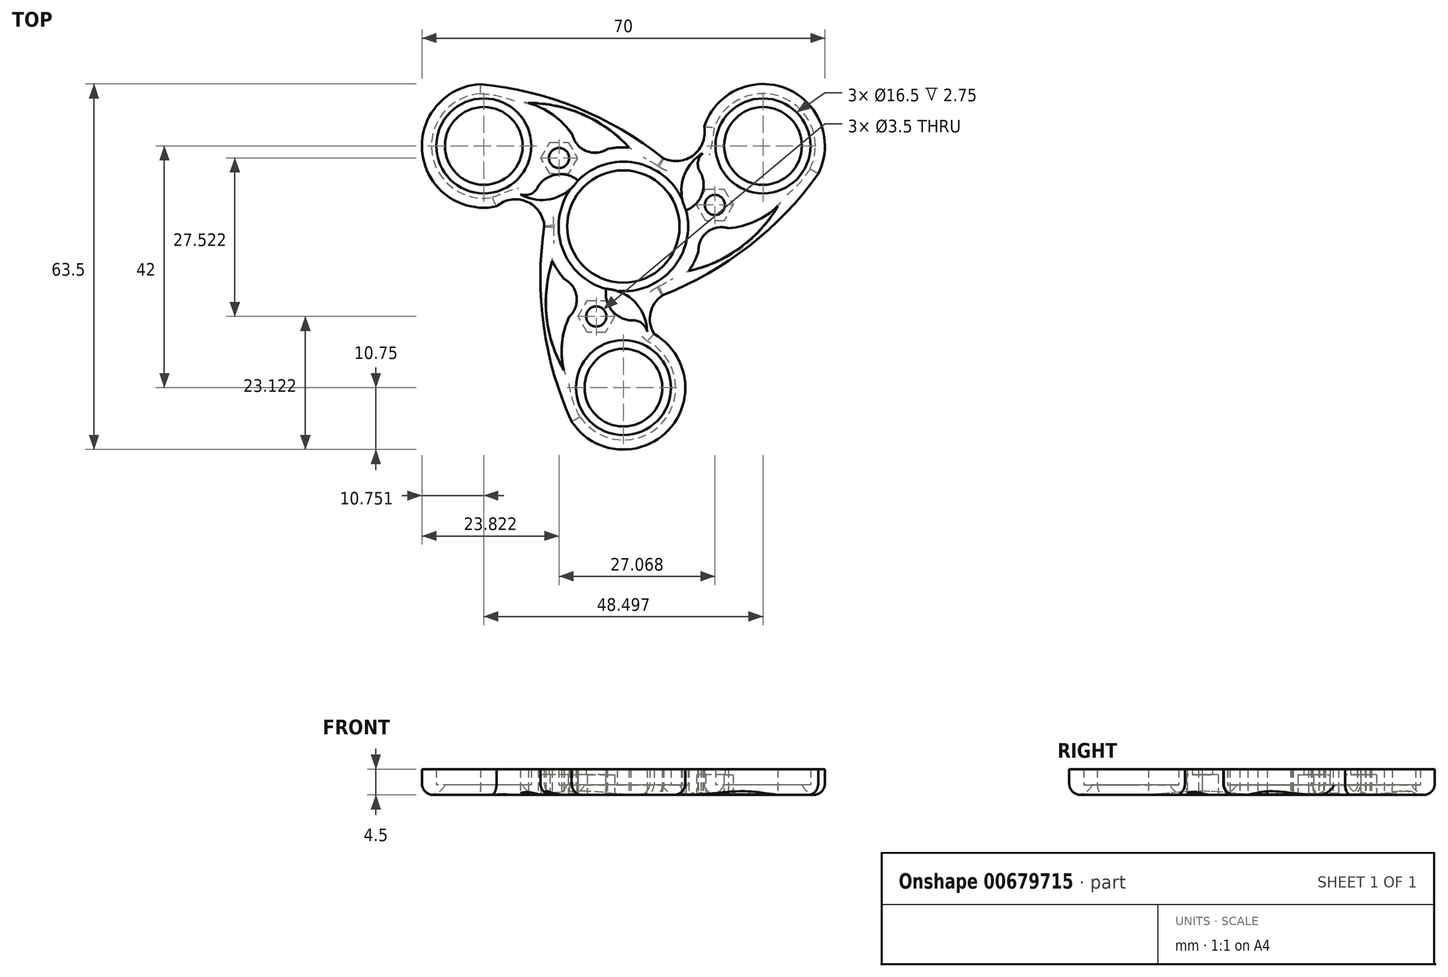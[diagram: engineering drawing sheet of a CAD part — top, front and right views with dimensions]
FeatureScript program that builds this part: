
annotation { "Feature Type Name" : "Feature", "Feature Type Description" : "" }
export const myFeature = defineFeature(function(context is Context, id is Id, definition is map)
    precondition{}
    {
        {
            assignVariable(context, id + "F0", {"name" : "OuterBearingHeight", "anyValue" : 5});
        }
        {
            assignVariable(context, id + "F1", {"name" : "CenterBearingHeight", "anyValue" : 7});
        }
        {
            var Q0;
            Q0=qCreatedBy(makeId("Top.planeOp"),FACE);
            var sketch = newSketch(context, id + "F2", { "sketchPlane" : qUnion([Q0])});
            skCircle(sketch, "E0", {"center": v(0, 0) * mm, "radius": 11.25 * mm});
            skCircle(sketch, "E1", {"center": v(0, 0) * mm, "radius": 9.75 * mm});
            skCircle(sketch, "E2", {"center": v(0, 0) * mm, "radius": 13.75 * mm});
            skCircle(sketch, "E3", {"center": v(0, -28) * mm, "radius": 10.75 * mm});
            skArc(sketch, "E4", {"start": v(-13.75, 0) * mm, "mid": v(-13.84, -17.29) * mm, "end": v(-9, -33.88) * mm});
            skArc(sketch, "E5", {"start": v(6.75, -11.98) * mm, "mid": v(4.65, -16.78) * mm, "end": v(8, -20.82) * mm});
            skPoint(sketch, "E6.center", {"position": v(0.04, 0.07) * mm});
            skCircle(sketch, "E7.cCircle", {"center": v(-4.71, -15.63) * mm, "radius": 2.75 * mm, "construction": true});
            skLineSegment(sketch, "E7.0", {"start": v(-3.12, -18.38) * mm, "end": v(-6.3, -18.38) * mm});
            skLineSegment(sketch, "E7.1", {"start": v(-6.3, -18.38) * mm, "end": v(-7.89, -15.63) * mm});
            skLineSegment(sketch, "E7.2", {"start": v(-7.89, -15.63) * mm, "end": v(-6.3, -12.88) * mm});
            skLineSegment(sketch, "E7.3", {"start": v(-6.3, -12.88) * mm, "end": v(-3.12, -12.88) * mm});
            skLineSegment(sketch, "E7.4", {"start": v(-3.12, -12.88) * mm, "end": v(-1.54, -15.63) * mm});
            skLineSegment(sketch, "E7.5", {"start": v(-1.54, -15.63) * mm, "end": v(-3.12, -18.38) * mm});
            skPoint(sketch, "E7.0.midPoint", {"position": v(-4.71, -18.38) * mm});
            skLineSegment(sketch, "E8", {"start": v(-4.71, -15.63) * mm, "end": v(-4.71, -12.92) * mm, "construction": true});
            skLineSegment(sketch, "E9", {"start": v(-4.71, -15.63) * mm, "end": v(-4.71, -18.34) * mm, "construction": true});
            skLineSegment(sketch, "E10", {"start": v(-4.71, -15.63) * mm, "end": v(-14.05, -15.63) * mm, "construction": true});
            skLineSegment(sketch, "E11", {"start": v(-4.71, -15.63) * mm, "end": v(4.63, -15.63) * mm, "construction": true});
            skCircle(sketch, "E12", {"center": v(-4.71, -15.63) * mm, "radius": 1.75 * mm});
            skArc(sketch, "E13", {"start": v(-12.37, -6) * mm, "mid": v(-13.33, -15.72) * mm, "end": v(-10.33, -25.02) * mm});
            skArc(sketch, "E14", {"start": v(-9.38, -15.63) * mm, "mid": v(-10.67, -20.24) * mm, "end": v(-10.33, -25.02) * mm});
            skArc(sketch, "E15", {"start": v(-9.38, -15.63) * mm, "mid": v(-8.13, -12.14) * mm, "end": v(-10.29, -9.12) * mm});
            skArc(sketch, "E16", {"start": v(4.11, -18.27) * mm, "mid": v(2.02, -13.15) * mm, "end": v(-3, -10.84) * mm});
            skArc(sketch, "E17", {"start": v(4.11, -18.27) * mm, "mid": v(3.08, -16.71) * mm, "end": v(1.26, -16.32) * mm});
            skArc(sketch, "E18", {"start": v(-3, -10.84) * mm, "mid": v(-2.06, -14.5) * mm, "end": v(1.26, -16.32) * mm});
            skCircle(sketch, "E19", {"center": v(0, -28) * mm, "radius": 8.25 * mm});
            skCircle(sketch, "E20", {"center": v(0, -28) * mm, "radius": 6.75 * mm});
            skArc(sketch, "E21.1.0", {"start": v(11.38, -7.71) * mm, "mid": v(20.28, -3.68) * mm, "end": v(26.83, 3.56) * mm});
            skLineSegment(sketch, "E21.1.1", {"start": v(17.48, 0.98) * mm, "end": v(14.3, 0.98) * mm});
            skLineSegment(sketch, "E21.1.2", {"start": v(14.3, 0.98) * mm, "end": v(12.71, 3.73) * mm});
            skCircle(sketch, "E21.1.3", {"center": v(15.89, 3.73) * mm, "radius": 2.75 * mm, "construction": true});
            skCircle(sketch, "E21.1.4", {"center": v(15.89, 3.73) * mm, "radius": 1.75 * mm});
            skLineSegment(sketch, "E21.1.5", {"start": v(19.07, 3.73) * mm, "end": v(17.48, 0.98) * mm});
            skLineSegment(sketch, "E21.1.6", {"start": v(17.48, 6.48) * mm, "end": v(19.07, 3.73) * mm});
            skLineSegment(sketch, "E21.1.7", {"start": v(14.3, 6.48) * mm, "end": v(17.48, 6.48) * mm});
            skLineSegment(sketch, "E21.1.8", {"start": v(12.71, 3.73) * mm, "end": v(14.3, 6.48) * mm});
            skArc(sketch, "E21.1.9", {"start": v(10.89, 2.82) * mm, "mid": v(13.6, 5.47) * mm, "end": v(13.5, 9.25) * mm});
            skArc(sketch, "E21.1.10", {"start": v(13.76, 12.7) * mm, "mid": v(10.38, 8.33) * mm, "end": v(10.89, 2.82) * mm});
            skArc(sketch, "E21.1.11", {"start": v(7, 11.84) * mm, "mid": v(12.2, 12.42) * mm, "end": v(14.03, 17.34) * mm});
            skCircle(sketch, "E21.1.12", {"center": v(24.25, 14) * mm, "radius": 10.75 * mm});
            skCircle(sketch, "E21.1.13", {"center": v(24.25, 14) * mm, "radius": 8.25 * mm});
            skCircle(sketch, "E21.1.14", {"center": v(24.25, 14) * mm, "radius": 6.75 * mm});
            skArc(sketch, "E21.1.15", {"start": v(13.76, 12.7) * mm, "mid": v(12.93, 11.02) * mm, "end": v(13.5, 9.25) * mm});
            skArc(sketch, "E21.1.16", {"start": v(6.87, -11.9) * mm, "mid": v(21.89, -3.34) * mm, "end": v(33.84, 9.15) * mm});
            skArc(sketch, "E21.1.17", {"start": v(18.22, -0.31) * mm, "mid": v(14.58, -0.98) * mm, "end": v(13.04, -4.35) * mm});
            skArc(sketch, "E21.1.18", {"start": v(18.22, -0.31) * mm, "mid": v(22.86, 0.88) * mm, "end": v(26.83, 3.56) * mm});
            skArc(sketch, "E21.2.0", {"start": v(1, 13.71) * mm, "mid": v(-6.95, 19.4) * mm, "end": v(-16.5, 21.45) * mm});
            skLineSegment(sketch, "E21.2.1", {"start": v(-9.6, 14.64) * mm, "end": v(-8, 11.9) * mm});
            skLineSegment(sketch, "E21.2.2", {"start": v(-8, 11.9) * mm, "end": v(-9.6, 9.14) * mm});
            skCircle(sketch, "E21.2.3", {"center": v(-11.18, 11.9) * mm, "radius": 2.75 * mm, "construction": true});
            skCircle(sketch, "E21.2.4", {"center": v(-11.18, 11.9) * mm, "radius": 1.75 * mm});
            skLineSegment(sketch, "E21.2.5", {"start": v(-12.77, 14.64) * mm, "end": v(-9.6, 14.64) * mm});
            skLineSegment(sketch, "E21.2.6", {"start": v(-14.35, 11.9) * mm, "end": v(-12.77, 14.64) * mm});
            skLineSegment(sketch, "E21.2.7", {"start": v(-12.77, 9.14) * mm, "end": v(-14.35, 11.9) * mm});
            skLineSegment(sketch, "E21.2.8", {"start": v(-9.6, 9.14) * mm, "end": v(-12.77, 9.14) * mm});
            skArc(sketch, "E21.2.9", {"start": v(-7.89, 8.02) * mm, "mid": v(-11.53, 9.04) * mm, "end": v(-14.76, 7.07) * mm});
            skArc(sketch, "E21.2.10", {"start": v(-17.87, 5.57) * mm, "mid": v(-12.4, 4.82) * mm, "end": v(-7.89, 8.02) * mm});
            skArc(sketch, "E21.2.11", {"start": v(-13.75, 0.14) * mm, "mid": v(-16.86, 4.36) * mm, "end": v(-22.03, 3.48) * mm});
            skCircle(sketch, "E21.2.12", {"center": v(-24.25, 14) * mm, "radius": 10.75 * mm});
            skCircle(sketch, "E21.2.13", {"center": v(-24.25, 14) * mm, "radius": 8.25 * mm});
            skCircle(sketch, "E21.2.14", {"center": v(-24.25, 14) * mm, "radius": 6.75 * mm});
            skArc(sketch, "E21.2.15", {"start": v(-17.87, 5.57) * mm, "mid": v(-16.01, 5.7) * mm, "end": v(-14.76, 7.07) * mm});
            skArc(sketch, "E21.2.16", {"start": v(6.87, 11.9) * mm, "mid": v(-8.05, 20.63) * mm, "end": v(-24.84, 24.73) * mm});
            skArc(sketch, "E21.2.17", {"start": v(-8.84, 15.94) * mm, "mid": v(-6.44, 13.11) * mm, "end": v(-2.75, 13.47) * mm});
            skArc(sketch, "E21.2.18", {"start": v(-8.84, 15.94) * mm, "mid": v(-12.2, 19.36) * mm, "end": v(-16.5, 21.45) * mm});
            skSolve(sketch);
        }
        {
            var Q0;
            {var subQ0=sQuery(id+"F2.wireOp",EDGE,"E7.1");Q0=makeQuery(id+"F2.imprint","IMPRINT",FACE,{"disambiguationData":[TD([[makeQuery(id+"F2.imprint","IMPRINT",EDGE,{"derivedFrom":subQ0}),1.0]])]});}
            var Q1;
            {var subQ5=sQuery(id+"F2.wireOp",EDGE,"E5");Q1=makeQuery(id+"F2.imprint","IMPRINT",FACE,{"disambiguationData":[TD([[makeQuery(id+"F2.imprint","IMPRINT",EDGE,{"derivedFrom":subQ5}),-1.0]])]});}
            var Q2;
            {var subQ0=sQuery(id+"F2.wireOp",EDGE,"f691ac80-1c01-42f0-a88e-231e112aa074.1.8");Q2=makeQuery(id+"F2.imprint","IMPRINT",FACE,{"disambiguationData":[TD([[makeQuery(id+"F2.imprint","IMPRINT",EDGE,{"derivedFrom":subQ0}),1.0]])]});}
            var Q3;
            {var subQ1=sQuery(id+"F2.wireOp",EDGE,"f691ac80-1c01-42f0-a88e-231e112aa074.1.0");Q3=makeQuery(id+"F2.imprint","IMPRINT",FACE,{"disambiguationData":[TD([[makeQuery(id+"F2.imprint","IMPRINT",EDGE,{"derivedFrom":subQ1}),-1.0]])]});}
            var Q4;
            {var subQ0=sQuery(id+"F2.wireOp",EDGE,"f691ac80-1c01-42f0-a88e-231e112aa074.2.8");Q4=makeQuery(id+"F2.imprint","IMPRINT",FACE,{"disambiguationData":[TD([[makeQuery(id+"F2.imprint","IMPRINT",EDGE,{"derivedFrom":subQ0}),1.0]])]});}
            var Q5;
            Q5=makeQuery(id+"F2.imprint","IMPRINT",FACE,{"disambiguationData":[TD([[makeQuery(id+"F2.imprint","IMPRINT",EDGE,{"derivedFrom":sQuery(id+"F2.wireOp",EDGE,"f691ac80-1c01-42f0-a88e-231e112aa074.2.2")}),-1.0]])]});
            var Q6;
            Q6=makeQuery(id+"F2.imprint","IMPRINT",FACE,{"disambiguationData":[TD([[makeQuery(id+"F2.imprint","IMPRINT",EDGE,{"derivedFrom":sQuery(id+"F2.wireOp",EDGE,"f691ac80-1c01-42f0-a88e-231e112aa074.1.2")}),-1.0]])]});
            var Q7;
            {var subQ1=sQuery(id+"F2.wireOp",EDGE,"f691ac80-1c01-42f0-a88e-231e112aa074.2.0");Q7=makeQuery(id+"F2.imprint","IMPRINT",FACE,{"disambiguationData":[TD([[makeQuery(id+"F2.imprint","IMPRINT",EDGE,{"derivedFrom":subQ1}),-1.0]])]});}
            var Q8;
            Q8=makeQuery(id+"F2.imprint","IMPRINT",FACE,{"disambiguationData":[TD([[makeQuery(id+"F2.imprint","IMPRINT",EDGE,{"derivedFrom":sQuery(id+"F2.wireOp",EDGE,"aKZDALUb-4dyq-ynNd-1TMt-uQF9IDW9dU3x")}),-1.0]])]});
            var Q9;
            {var subQ0=sQuery(id+"F2.wireOp",EDGE,"BNeyDjp7-idxR-Yro0-WZsy-1JtXtv3nSXo7");Q9=makeQuery(id+"F2.imprint","IMPRINT",FACE,{"disambiguationData":[TD([[makeQuery(id+"F2.imprint","IMPRINT",EDGE,{"derivedFrom":subQ0}),1.0]])]});}
            var Q10;
            {var subQ0=sQuery(id+"F2.wireOp",EDGE,"8gaKkmaj-PT3W-1uV4-PrTw-aFj1ESdI5pcj");var subQ1=sQuery(id+"F2.wireOp",EDGE,"E4");var subQ2=makeQuery(id+"F2.imprint","INTERSECT",VERTEX,{"disambiguationData":[OD(0.0)],"derivedFrom":[subQ1,subQ0]});Q10=makeQuery(id+"F2.imprint","IMPRINT",FACE,{"disambiguationData":[TD([[makeQuery(id+"F2.imprint","IMPRINT",EDGE,{"disambiguationData":[TD([[subQ2,-1.0]])],"derivedFrom":subQ1}),-1.0]])]});}
            var Q11;
            {var subQ3=sQuery(id+"F2.wireOp",EDGE,"E13");Q11=makeQuery(id+"F2.imprint","IMPRINT",FACE,{"disambiguationData":[TD([[makeQuery(id+"F2.imprint","IMPRINT",EDGE,{"derivedFrom":subQ3}),-1.0]])]});}
            var Q12;
            {var subQ5=sQuery(id+"F2.wireOp",EDGE,"yW5sj1OK-dV5J-gnst-7nq6-E0PAgaZ6P3tT");Q12=makeQuery(id+"F2.imprint","IMPRINT",FACE,{"disambiguationData":[TD([[makeQuery(id+"F2.imprint","IMPRINT",EDGE,{"derivedFrom":subQ5}),1.0]])]});}
            var Q13;
            {var subQ0=sQuery(id+"F2.wireOp",EDGE,"E5");var subQ1=sQuery(id+"F2.wireOp",EDGE,"E3");var subQ2=makeQuery(id+"F2.imprint","INTERSECT",VERTEX,{"disambiguationData":[OD(0.0)],"derivedFrom":[subQ1,subQ0]});Q13=makeQuery(id+"F2.imprint","IMPRINT",FACE,{"disambiguationData":[TD([[makeQuery(id+"F2.imprint","IMPRINT",EDGE,{"disambiguationData":[TD([[subQ2,-1.0]])],"derivedFrom":subQ1}),1.0]])]});}
            var Q14;
            {var subQ1=sQuery(id+"F2.wireOp",EDGE,"E7.4");var subQ3=sQuery(id+"F2.wireOp",EDGE,"E2");var subQ4=makeQuery(id+"F2.imprint","INTERSECT",VERTEX,{"derivedFrom":[subQ3,subQ1]});Q14=makeQuery(id+"F2.imprint","IMPRINT",FACE,{"disambiguationData":[TD([[makeQuery(id+"F2.imprint","IMPRINT",EDGE,{"disambiguationData":[TD([[subQ4,-1.0]])],"derivedFrom":subQ3}),-1.0]])]});}
            var Q15;
            {var subQ0=sQuery(id+"F2.wireOp",EDGE,"E16");var subQ1=sQuery(id+"F2.wireOp",EDGE,"E5");var subQ2=makeQuery(id+"F2.imprint","INTERSECT",VERTEX,{"disambiguationData":[OD(0.0)],"derivedFrom":[subQ1,subQ0]});Q15=makeQuery(id+"F2.imprint","IMPRINT",FACE,{"disambiguationData":[TD([[makeQuery(id+"F2.imprint","IMPRINT",EDGE,{"disambiguationData":[TD([[subQ2,-1.0]])],"derivedFrom":subQ1}),1.0]])]});}
            var Q16;
            Q16=makeQuery(id+"F2.imprint","IMPRINT",FACE,{"disambiguationData":[TD([[makeQuery(id+"F2.imprint","IMPRINT",EDGE,{"derivedFrom":sQuery(id+"F2.wireOp",EDGE,"E19")}),-1.0]])]});
            var Q17;
            {var subQ3=sQuery(id+"F2.wireOp",EDGE,"E2");var subQ7=makeQuery(id+"F2.imprint","INTERSECT",VERTEX,{"derivedFrom":[subQ3,sQuery(id+"F2.wireOp",EDGE,"E4")]});Q17=makeQuery(id+"F2.imprint","IMPRINT",FACE,{"disambiguationData":[TD([[makeQuery(id+"F2.imprint","IMPRINT",EDGE,{"disambiguationData":[TD([[subQ7,-1.0]])],"derivedFrom":subQ3}),1.0]])]});}
            var Q18;
            {var subQ1=sQuery(id+"F2.wireOp",EDGE,"E2");var subQ5=sQuery(id+"F2.wireOp",EDGE,"E21.1.8");var subQ15=makeQuery(id+"F2.imprint","INTERSECT",VERTEX,{"derivedFrom":[subQ1,subQ5]});Q18=makeQuery(id+"F2.imprint","IMPRINT",FACE,{"disambiguationData":[TD([[makeQuery(id+"F2.imprint","IMPRINT",EDGE,{"disambiguationData":[TD([[subQ15,-1.0]])],"derivedFrom":subQ1}),1.0]])]});}
            var Q19;
            {var subQ0=sQuery(id+"F2.wireOp",EDGE,"E21.1.0");Q19=makeQuery(id+"F2.imprint","IMPRINT",FACE,{"disambiguationData":[TD([[makeQuery(id+"F2.imprint","IMPRINT",EDGE,{"derivedFrom":subQ0}),-1.0]])]});}
            var Q20;
            {var subQ6=sQuery(id+"F2.wireOp",EDGE,"E21.1.1");Q20=makeQuery(id+"F2.imprint","IMPRINT",FACE,{"disambiguationData":[TD([[makeQuery(id+"F2.imprint","IMPRINT",EDGE,{"derivedFrom":subQ6}),1.0]])]});}
            var Q21;
            {var subQ3=sQuery(id+"F2.wireOp",EDGE,"E2");var subQ5=sQuery(id+"F2.wireOp",EDGE,"E21.1.8");var subQ6=makeQuery(id+"F2.imprint","INTERSECT",VERTEX,{"derivedFrom":[subQ3,subQ5]});Q21=makeQuery(id+"F2.imprint","IMPRINT",FACE,{"disambiguationData":[TD([[makeQuery(id+"F2.imprint","IMPRINT",EDGE,{"disambiguationData":[TD([[subQ6,-1.0]])],"derivedFrom":subQ3}),-1.0]])]});}
            var Q22;
            {var subQ0=sQuery(id+"F2.wireOp",EDGE,"E21.1.11");var subQ1=sQuery(id+"F2.wireOp",EDGE,"E2");var subQ2=makeQuery(id+"F2.imprint","INTERSECT",VERTEX,{"derivedFrom":[subQ1,subQ0]});Q22=makeQuery(id+"F2.imprint","IMPRINT",FACE,{"disambiguationData":[TD([[makeQuery(id+"F2.imprint","IMPRINT",EDGE,{"disambiguationData":[TD([[subQ2,1.0]])],"derivedFrom":subQ1}),-1.0]])]});}
            var Q23;
            {var subQ3=sQuery(id+"F2.wireOp",EDGE,"E2");var subQ16=makeQuery(id+"F2.imprint","INTERSECT",VERTEX,{"derivedFrom":[subQ3,sQuery(id+"F2.wireOp",EDGE,"E21.1.11")]});Q23=makeQuery(id+"F2.imprint","IMPRINT",FACE,{"disambiguationData":[TD([[makeQuery(id+"F2.imprint","IMPRINT",EDGE,{"disambiguationData":[TD([[subQ16,1.0]])],"derivedFrom":subQ3}),1.0]])]});}
            var Q24;
            Q24=makeQuery(id+"F2.imprint","IMPRINT",FACE,{"disambiguationData":[TD([[makeQuery(id+"F2.imprint","IMPRINT",EDGE,{"derivedFrom":sQuery(id+"F2.wireOp",EDGE,"E21.1.13")}),-1.0]])]});
            var Q25;
            Q25=makeQuery(id+"F2.imprint","IMPRINT",FACE,{"disambiguationData":[TD([[makeQuery(id+"F2.imprint","IMPRINT",EDGE,{"derivedFrom":sQuery(id+"F2.wireOp",EDGE,"E21.2.13")}),-1.0]])]});
            var Q26;
            {var subQ1=sQuery(id+"F2.wireOp",EDGE,"E21.2.1");Q26=makeQuery(id+"F2.imprint","IMPRINT",FACE,{"disambiguationData":[TD([[makeQuery(id+"F2.imprint","IMPRINT",EDGE,{"derivedFrom":subQ1}),1.0]])]});}
            var Q27;
            {var subQ0=sQuery(id+"F2.wireOp",EDGE,"E21.2.0");Q27=makeQuery(id+"F2.imprint","IMPRINT",FACE,{"disambiguationData":[TD([[makeQuery(id+"F2.imprint","IMPRINT",EDGE,{"derivedFrom":subQ0}),-1.0]])]});}
            var Q28;
            {var subQ0=sQuery(id+"F2.wireOp",EDGE,"E21.2.11");var subQ1=sQuery(id+"F2.wireOp",EDGE,"E2");var subQ2=makeQuery(id+"F2.imprint","INTERSECT",VERTEX,{"derivedFrom":[subQ1,subQ0]});Q28=makeQuery(id+"F2.imprint","IMPRINT",FACE,{"disambiguationData":[TD([[makeQuery(id+"F2.imprint","IMPRINT",EDGE,{"disambiguationData":[TD([[subQ2,1.0]])],"derivedFrom":subQ1}),-1.0]])]});}
            var Q29;
            {var subQ0=sQuery(id+"F2.wireOp",EDGE,"E21.2.8");var subQ3=sQuery(id+"F2.wireOp",EDGE,"E2");var subQ4=makeQuery(id+"F2.imprint","INTERSECT",VERTEX,{"derivedFrom":[subQ3,subQ0]});Q29=makeQuery(id+"F2.imprint","IMPRINT",FACE,{"disambiguationData":[TD([[makeQuery(id+"F2.imprint","IMPRINT",EDGE,{"disambiguationData":[TD([[subQ4,-1.0]])],"derivedFrom":subQ3}),-1.0]])]});}
            extrude(context, id + "F3", {"entities" : qUnion([Q0, Q1, Q2, Q3, Q4, Q5, Q6, Q7, Q8, Q9, Q10, Q11, Q12, Q13, Q14, Q15, Q16, Q17, Q18, Q19, Q20, Q21, Q22, Q23, Q24, Q25, Q26, Q27, Q28, Q29]), "depth" : ((getVariable(context, 'CenterBearingHeight') / 2) + 1) * mm, "offsetDistance" : 25 * mm});
        }
        {
            var Q0;
            Q0=makeQuery(id+"F2.imprint","IMPRINT",FACE,{"disambiguationData":[TD([[makeQuery(id+"F2.imprint","IMPRINT",EDGE,{"derivedFrom":sQuery(id+"F2.wireOp",EDGE,"f691ac80-1c01-42f0-a88e-231e112aa074.2.2")}),1.0]])]});
            var Q1;
            Q1=makeQuery(id+"F2.imprint","IMPRINT",FACE,{"disambiguationData":[TD([[makeQuery(id+"F2.imprint","IMPRINT",EDGE,{"derivedFrom":sQuery(id+"F2.wireOp",EDGE,"f691ac80-1c01-42f0-a88e-231e112aa074.1.2")}),1.0]])]});
            var Q2;
            Q2=makeQuery(id+"F2.imprint","IMPRINT",FACE,{"disambiguationData":[TD([[makeQuery(id+"F2.imprint","IMPRINT",EDGE,{"derivedFrom":sQuery(id+"F2.wireOp",EDGE,"aKZDALUb-4dyq-ynNd-1TMt-uQF9IDW9dU3x")}),1.0]])]});
            var Q3;
            Q3=makeQuery(id+"F2.imprint","IMPRINT",FACE,{"disambiguationData":[TD([[makeQuery(id+"F2.imprint","IMPRINT",EDGE,{"derivedFrom":sQuery(id+"F2.wireOp",EDGE,"E19")}),1.0]])]});
            var Q4;
            Q4=makeQuery(id+"F2.imprint","IMPRINT",FACE,{"disambiguationData":[TD([[makeQuery(id+"F2.imprint","IMPRINT",EDGE,{"derivedFrom":sQuery(id+"F2.wireOp",EDGE,"E1")}),-1.0]])]});
            var Q5;
            Q5=makeQuery(id+"F2.imprint","IMPRINT",FACE,{"disambiguationData":[TD([[makeQuery(id+"F2.imprint","IMPRINT",EDGE,{"derivedFrom":sQuery(id+"F2.wireOp",EDGE,"E21.2.13")}),1.0]])]});
            var Q6;
            Q6=makeQuery(id+"F2.imprint","IMPRINT",FACE,{"disambiguationData":[TD([[makeQuery(id+"F2.imprint","IMPRINT",EDGE,{"derivedFrom":sQuery(id+"F2.wireOp",EDGE,"E21.1.13")}),1.0]])]});
            extrude(context, id + "F4", {"entities" : qUnion([Q0, Q1, Q2, Q3, Q4, Q5, Q6]), "operationType" : NewBodyOperationType.ADD, "depth" : (((getVariable(context, 'CenterBearingHeight') / 2) + .75) - getVariable(context, 'OuterBearingHeight') / 2) * mm, "offsetDistance" : 25 * mm});
        }
        {
            var Q0;
            {var subQ3=sQuery(id+"F2.wireOp",EDGE,"E2");var subQ5=sQuery(id+"F2.wireOp",EDGE,"E5");var subQ6=makeQuery(id+"F2.imprint","INTERSECT",VERTEX,{"derivedFrom":[subQ3,subQ5]});Q0=makeQuery(id+"F2.imprint","IMPRINT",FACE,{"disambiguationData":[TD([[makeQuery(id+"F2.imprint","IMPRINT",EDGE,{"disambiguationData":[TD([[subQ6,1.0]])],"derivedFrom":subQ3}),-1.0]])]});}
            var Q1;
            {var subQ0=sQuery(id+"F2.wireOp",EDGE,"E7.1");Q1=makeQuery(id+"F2.imprint","IMPRINT",FACE,{"disambiguationData":[TD([[makeQuery(id+"F2.imprint","IMPRINT",EDGE,{"derivedFrom":subQ0}),-1.0]])]});}
            var Q2;
            {var subQ0=sQuery(id+"F2.wireOp",EDGE,"E7.3");var subQ1=sQuery(id+"F2.wireOp",EDGE,"E2");var subQ2=makeQuery(id+"F2.imprint","INTERSECT",VERTEX,{"derivedFrom":[subQ1,subQ0]});Q2=makeQuery(id+"F2.imprint","IMPRINT",FACE,{"disambiguationData":[TD([[makeQuery(id+"F2.imprint","IMPRINT",EDGE,{"disambiguationData":[TD([[subQ2,-1.0]])],"derivedFrom":subQ1}),1.0]])]});}
            var Q3;
            {var subQ0=sQuery(id+"F2.wireOp",EDGE,"E7.5");var subQ1=sQuery(id+"F2.wireOp",EDGE,"E3");var subQ2=makeQuery(id+"F2.imprint","INTERSECT",VERTEX,{"derivedFrom":[subQ1,subQ0]});Q3=makeQuery(id+"F2.imprint","IMPRINT",FACE,{"disambiguationData":[TD([[makeQuery(id+"F2.imprint","IMPRINT",EDGE,{"disambiguationData":[TD([[subQ2,-1.0]])],"derivedFrom":subQ1}),1.0]])]});}
            var Q4;
            {var subQ1=sQuery(id+"F2.wireOp",EDGE,"E21.2.1");Q4=makeQuery(id+"F2.imprint","IMPRINT",FACE,{"disambiguationData":[TD([[makeQuery(id+"F2.imprint","IMPRINT",EDGE,{"derivedFrom":subQ1}),-1.0]])]});}
            var Q5;
            {var subQ0=sQuery(id+"F2.wireOp",EDGE,"E21.2.2");var subQ1=sQuery(id+"F2.wireOp",EDGE,"E2");var subQ2=makeQuery(id+"F2.imprint","INTERSECT",VERTEX,{"derivedFrom":[subQ1,subQ0]});Q5=makeQuery(id+"F2.imprint","IMPRINT",FACE,{"disambiguationData":[TD([[makeQuery(id+"F2.imprint","IMPRINT",EDGE,{"disambiguationData":[TD([[subQ2,-1.0]])],"derivedFrom":subQ1}),1.0]])]});}
            var Q6;
            {var subQ0=sQuery(id+"F2.wireOp",EDGE,"E21.2.7");var subQ1=sQuery(id+"F2.wireOp",EDGE,"E21.2.6");var subQ2=makeQuery(id+"F2.imprint","INTERSECT",VERTEX,{"derivedFrom":[subQ1,subQ0]});Q6=makeQuery(id+"F2.imprint","IMPRINT",FACE,{"disambiguationData":[TD([[makeQuery(id+"F2.imprint","IMPRINT",EDGE,{"disambiguationData":[TD([[subQ2,-1.0]])],"derivedFrom":subQ1}),-1.0]])]});}
            var Q7;
            {var subQ1=sQuery(id+"F2.wireOp",EDGE,"E21.1.1");Q7=makeQuery(id+"F2.imprint","IMPRINT",FACE,{"disambiguationData":[TD([[makeQuery(id+"F2.imprint","IMPRINT",EDGE,{"derivedFrom":subQ1}),-1.0]])]});}
            var Q8;
            {var subQ0=sQuery(id+"F2.wireOp",EDGE,"E21.1.7");var subQ1=sQuery(id+"F2.wireOp",EDGE,"E21.1.6");var subQ2=makeQuery(id+"F2.imprint","INTERSECT",VERTEX,{"derivedFrom":[subQ1,subQ0]});Q8=makeQuery(id+"F2.imprint","IMPRINT",FACE,{"disambiguationData":[TD([[makeQuery(id+"F2.imprint","IMPRINT",EDGE,{"disambiguationData":[TD([[subQ2,-1.0]])],"derivedFrom":subQ1}),-1.0]])]});}
            var Q9;
            {var subQ0=sQuery(id+"F2.wireOp",EDGE,"E21.1.8");var subQ1=sQuery(id+"F2.wireOp",EDGE,"E2");var subQ2=makeQuery(id+"F2.imprint","INTERSECT",VERTEX,{"derivedFrom":[subQ1,subQ0]});Q9=makeQuery(id+"F2.imprint","IMPRINT",FACE,{"disambiguationData":[TD([[makeQuery(id+"F2.imprint","IMPRINT",EDGE,{"disambiguationData":[TD([[subQ2,1.0]])],"derivedFrom":subQ1}),1.0]])]});}
            extrude(context, id + "F5", {"entities" : qUnion([Q0, Q1, Q2, Q3, Q4, Q5, Q6, Q7, Q8, Q9]), "operationType" : NewBodyOperationType.ADD, "depth" : ((getVariable(context, 'CenterBearingHeight') / 2) + 1) * mm, "offsetDistance" : 25 * mm, "hasSecondDirection" : true, "secondDirectionOppositeDirection" : false, "secondDirectionDepth" : 3.5 * mm});
        }
        {
            var Q0;
            Q0=makeQuery(id+"F2.imprint","IMPRINT",FACE,{"disambiguationData":[TD([[makeQuery(id+"F2.imprint","IMPRINT",EDGE,{"derivedFrom":sQuery(id+"F2.wireOp",EDGE,"E0")}),1.0]])]});
            extrude(context, id + "F6", {"entities" : qUnion([Q0]), "operationType" : NewBodyOperationType.ADD, "depth" : 1 * mm, "offsetDistance" : 25 * mm});
        }
        {
            var Q0;
            Q0=makeQuery(id+"F3.opExtrude","CAP_EDGE",EDGE,{"disambiguationData":[OSD([sQuery(id+"F2.wireOp",EDGE,"E21.2.12")])],"isStart":true});
            var Q1;
            Q1=makeQuery(id+"F3.opExtrude","CAP_EDGE",EDGE,{"disambiguationData":[OSD([sQuery(id+"F2.wireOp",EDGE,"E21.2.11")])],"isStart":true});
            var Q2;
            Q2=makeQuery(id+"F3.opExtrude","CAP_EDGE",EDGE,{"disambiguationData":[OSD([sQuery(id+"F2.wireOp",EDGE,"E21.2.16")])],"isStart":true});
            var Q3;
            Q3=makeQuery(id+"F3.opExtrude","CAP_EDGE",EDGE,{"disambiguationData":[OSD([sQuery(id+"F2.wireOp",EDGE,"E21.1.11")])],"isStart":true});
            var Q4;
            Q4=makeQuery(id+"F3.opExtrude","CAP_EDGE",EDGE,{"disambiguationData":[OSD([sQuery(id+"F2.wireOp",EDGE,"E21.1.12")])],"isStart":true});
            var Q5;
            Q5=makeQuery(id+"F3.opExtrude","CAP_EDGE",EDGE,{"disambiguationData":[OSD([sQuery(id+"F2.wireOp",EDGE,"E21.1.16")])],"isStart":true});
            var Q6;
            Q6=makeQuery(id+"F3.opExtrude","CAP_EDGE",EDGE,{"disambiguationData":[OSD([sQuery(id+"F2.wireOp",EDGE,"E5")])],"isStart":true});
            var Q7;
            Q7=makeQuery(id+"F3.opExtrude","CAP_EDGE",EDGE,{"disambiguationData":[OSD([sQuery(id+"F2.wireOp",EDGE,"E3")])],"isStart":true});
            var Q8;
            Q8=makeQuery(id+"F3.opExtrude","CAP_EDGE",EDGE,{"disambiguationData":[OSD([sQuery(id+"F2.wireOp",EDGE,"E4")])],"isStart":true});
            var Q9;
            {var subQ0=sQuery(id+"F2.wireOp",EDGE,"E2");Q9=makeQuery(id+"F3.opExtrude","CAP_EDGE",EDGE,{"disambiguationData":[OSD([subQ0]),TDD([makeQuery(id+"F2.imprint","IMPRINT",EDGE,{"disambiguationData":[TD([[makeQuery(id+"F2.imprint","INTERSECT",VERTEX,{"derivedFrom":[subQ0,sQuery(id+"F2.wireOp",EDGE,"E21.1.11")]}),-1.0]])],"derivedFrom":subQ0})])],"isStart":true});}
            var Q10;
            {var subQ0=sQuery(id+"F2.wireOp",EDGE,"E2");Q10=makeQuery(id+"F3.opExtrude","CAP_EDGE",EDGE,{"disambiguationData":[OSD([subQ0]),TDD([makeQuery(id+"F2.imprint","IMPRINT",EDGE,{"disambiguationData":[TD([[makeQuery(id+"F2.imprint","INTERSECT",VERTEX,{"derivedFrom":[subQ0,sQuery(id+"F2.wireOp",EDGE,"E5")]}),-1.0]])],"derivedFrom":subQ0})])],"isStart":true});}
            var Q11;
            {var subQ0=sQuery(id+"F2.wireOp",EDGE,"E2");Q11=makeQuery(id+"F3.opExtrude","CAP_EDGE",EDGE,{"disambiguationData":[OSD([subQ0]),TDD([makeQuery(id+"F2.imprint","IMPRINT",EDGE,{"disambiguationData":[TD([[makeQuery(id+"F2.imprint","INTERSECT",VERTEX,{"derivedFrom":[subQ0,sQuery(id+"F2.wireOp",EDGE,"E4")]}),1.0]])],"derivedFrom":subQ0})])],"isStart":true});}
            fillet(context, id + "F7", {"entities" : qUnion([Q0, Q1, Q2, Q3, Q4, Q5, Q6, Q7, Q8, Q9, Q10, Q11]), "radius" : 2 * mm, "tangentPropagation" : true, "allowEdgeOverflow" : false});
        }
        {
            var Q0;
            Q0=makeQuery(id+"F4.opExtrude","CAP_EDGE",EDGE,{"disambiguationData":[OSD([sQuery(id+"F2.wireOp",EDGE,"f691ac80-1c01-42f0-a88e-231e112aa074.2.3")])],"isStart":true});
            var Q1;
            Q1=makeQuery(id+"F6.opExtrude","CAP_EDGE",EDGE,{"disambiguationData":[OSD([sQuery(id+"F2.wireOp",EDGE,"E1")])],"isStart":true});
            var Q2;
            Q2=makeQuery(id+"F4.opExtrude","CAP_EDGE",EDGE,{"disambiguationData":[OSD([sQuery(id+"F2.wireOp",EDGE,"udslHx3o-LPzl-F921-wRQS-P6q11kkCxCmo")])],"isStart":true});
            var Q3;
            Q3=makeQuery(id+"F4.opExtrude","CAP_EDGE",EDGE,{"disambiguationData":[OSD([sQuery(id+"F2.wireOp",EDGE,"f691ac80-1c01-42f0-a88e-231e112aa074.1.3")])],"isStart":true});
            var Q4;
            Q4=makeQuery(id+"F4.opExtrude","CAP_EDGE",EDGE,{"disambiguationData":[OSD([sQuery(id+"F2.wireOp",EDGE,"E1")])],"isStart":true});
            var Q5;
            Q5=makeQuery(id+"F4.opExtrude","CAP_EDGE",EDGE,{"disambiguationData":[OSD([sQuery(id+"F2.wireOp",EDGE,"E21.2.14")])],"isStart":true});
            var Q6;
            Q6=makeQuery(id+"F4.opExtrude","CAP_EDGE",EDGE,{"disambiguationData":[OSD([sQuery(id+"F2.wireOp",EDGE,"E20")])],"isStart":true});
            var Q7;
            Q7=makeQuery(id+"F4.opExtrude","CAP_EDGE",EDGE,{"disambiguationData":[OSD([sQuery(id+"F2.wireOp",EDGE,"E21.1.14")])],"isStart":true});
            fillet(context, id + "F8", {"entities" : qUnion([Q0, Q1, Q2, Q3, Q4, Q5, Q6, Q7]), "radius" : 3 * mm, "tangentPropagation" : true, "allowEdgeOverflow" : false});
        }
        {
            var Q0;
            Q0=makeQuery(id+"F3.opExtrude","CAP_EDGE",EDGE,{"disambiguationData":[OSD([sQuery(id+"F2.wireOp",EDGE,"E21.1.17")])],"isStart":true});
            var Q1;
            {var subQ0=sQuery(id+"F2.wireOp",EDGE,"E2");Q1=makeQuery(id+"F3.opExtrude","CAP_EDGE",EDGE,{"disambiguationData":[OSD([subQ0]),TDD([makeQuery(id+"F2.imprint","IMPRINT",EDGE,{"disambiguationData":[TD([[makeQuery(id+"F2.imprint","INTERSECT",VERTEX,{"derivedFrom":[subQ0,sQuery(id+"F2.wireOp",EDGE,"E21.1.0")]}),-1.0]])],"derivedFrom":subQ0})])],"isStart":true});}
            var Q2;
            Q2=makeQuery(id+"F7.opFillet","BLEND_EDGE",EDGE,{"blendedFrom":[makeQuery(id+"F3.opExtrude","CAP_EDGE",EDGE,{"disambiguationData":[OSD([sQuery(id+"F2.wireOp",EDGE,"E21.1.16")])],"isStart":true}),makeQuery(id+"F3.opExtrude","SWEPT_FACE",FACE,{"disambiguationData":[OSD([sQuery(id+"F2.wireOp",EDGE,"E21.1.0")])]})],"blendedInto":[makeQuery(id+"F3.opExtrude","SWEPT_FACE",FACE,{"disambiguationData":[OSD([sQuery(id+"F2.wireOp",EDGE,"E21.1.0")])]})]});
            var Q3;
            Q3=makeQuery(id+"F3.opExtrude","CAP_EDGE",EDGE,{"disambiguationData":[OSD([sQuery(id+"F2.wireOp",EDGE,"E21.1.18")])],"isStart":true});
            var Q4;
            Q4=makeQuery(id+"F3.opExtrude","CAP_EDGE",EDGE,{"disambiguationData":[OSD([sQuery(id+"F2.wireOp",EDGE,"E15")])],"isStart":true});
            var Q5;
            {var subQ0=sQuery(id+"F2.wireOp",EDGE,"E2");Q5=makeQuery(id+"F3.opExtrude","CAP_EDGE",EDGE,{"disambiguationData":[OSD([subQ0]),TDD([makeQuery(id+"F2.imprint","IMPRINT",EDGE,{"disambiguationData":[TD([[makeQuery(id+"F2.imprint","INTERSECT",VERTEX,{"derivedFrom":[subQ0,sQuery(id+"F2.wireOp",EDGE,"E13")]}),-1.0]])],"derivedFrom":subQ0})])],"isStart":true});}
            var Q6;
            Q6=makeQuery(id+"F7.opFillet","BLEND_EDGE",EDGE,{"blendedFrom":[makeQuery(id+"F3.opExtrude","CAP_EDGE",EDGE,{"disambiguationData":[OSD([sQuery(id+"F2.wireOp",EDGE,"E4")])],"isStart":true}),makeQuery(id+"F3.opExtrude","SWEPT_FACE",FACE,{"disambiguationData":[OSD([sQuery(id+"F2.wireOp",EDGE,"E13")])]})],"blendedInto":[makeQuery(id+"F3.opExtrude","SWEPT_FACE",FACE,{"disambiguationData":[OSD([sQuery(id+"F2.wireOp",EDGE,"E13")])]})]});
            var Q7;
            Q7=makeQuery(id+"F3.opExtrude","CAP_EDGE",EDGE,{"disambiguationData":[OSD([sQuery(id+"F2.wireOp",EDGE,"E14")])],"isStart":true});
            var Q8;
            Q8=makeQuery(id+"F3.opExtrude","CAP_EDGE",EDGE,{"disambiguationData":[OSD([sQuery(id+"F2.wireOp",EDGE,"E21.2.17")])],"isStart":true});
            var Q9;
            Q9=makeQuery(id+"F3.opExtrude","CAP_EDGE",EDGE,{"disambiguationData":[OSD([sQuery(id+"F2.wireOp",EDGE,"E21.2.18")])],"isStart":true});
            var Q10;
            Q10=makeQuery(id+"F7.opFillet","BLEND_EDGE",EDGE,{"blendedFrom":[makeQuery(id+"F3.opExtrude","CAP_EDGE",EDGE,{"disambiguationData":[OSD([sQuery(id+"F2.wireOp",EDGE,"E21.2.16")])],"isStart":true}),makeQuery(id+"F3.opExtrude","SWEPT_FACE",FACE,{"disambiguationData":[OSD([sQuery(id+"F2.wireOp",EDGE,"E21.2.0")])]})],"blendedInto":[makeQuery(id+"F3.opExtrude","SWEPT_FACE",FACE,{"disambiguationData":[OSD([sQuery(id+"F2.wireOp",EDGE,"E21.2.0")])]})]});
            var Q11;
            {var subQ0=sQuery(id+"F2.wireOp",EDGE,"E2");Q11=makeQuery(id+"F3.opExtrude","CAP_EDGE",EDGE,{"disambiguationData":[OSD([subQ0]),TDD([makeQuery(id+"F2.imprint","IMPRINT",EDGE,{"disambiguationData":[TD([[makeQuery(id+"F2.imprint","INTERSECT",VERTEX,{"derivedFrom":[subQ0,sQuery(id+"F2.wireOp",EDGE,"E21.2.0")]}),-1.0]])],"derivedFrom":subQ0})])],"isStart":true});}
            chamfer(context, id + "F9", {"entities" : qUnion([Q0, Q1, Q2, Q3, Q4, Q5, Q6, Q7, Q8, Q9, Q10, Q11]), "width" : .1 * mm, "tangentPropagation" : true});
        }
    });
